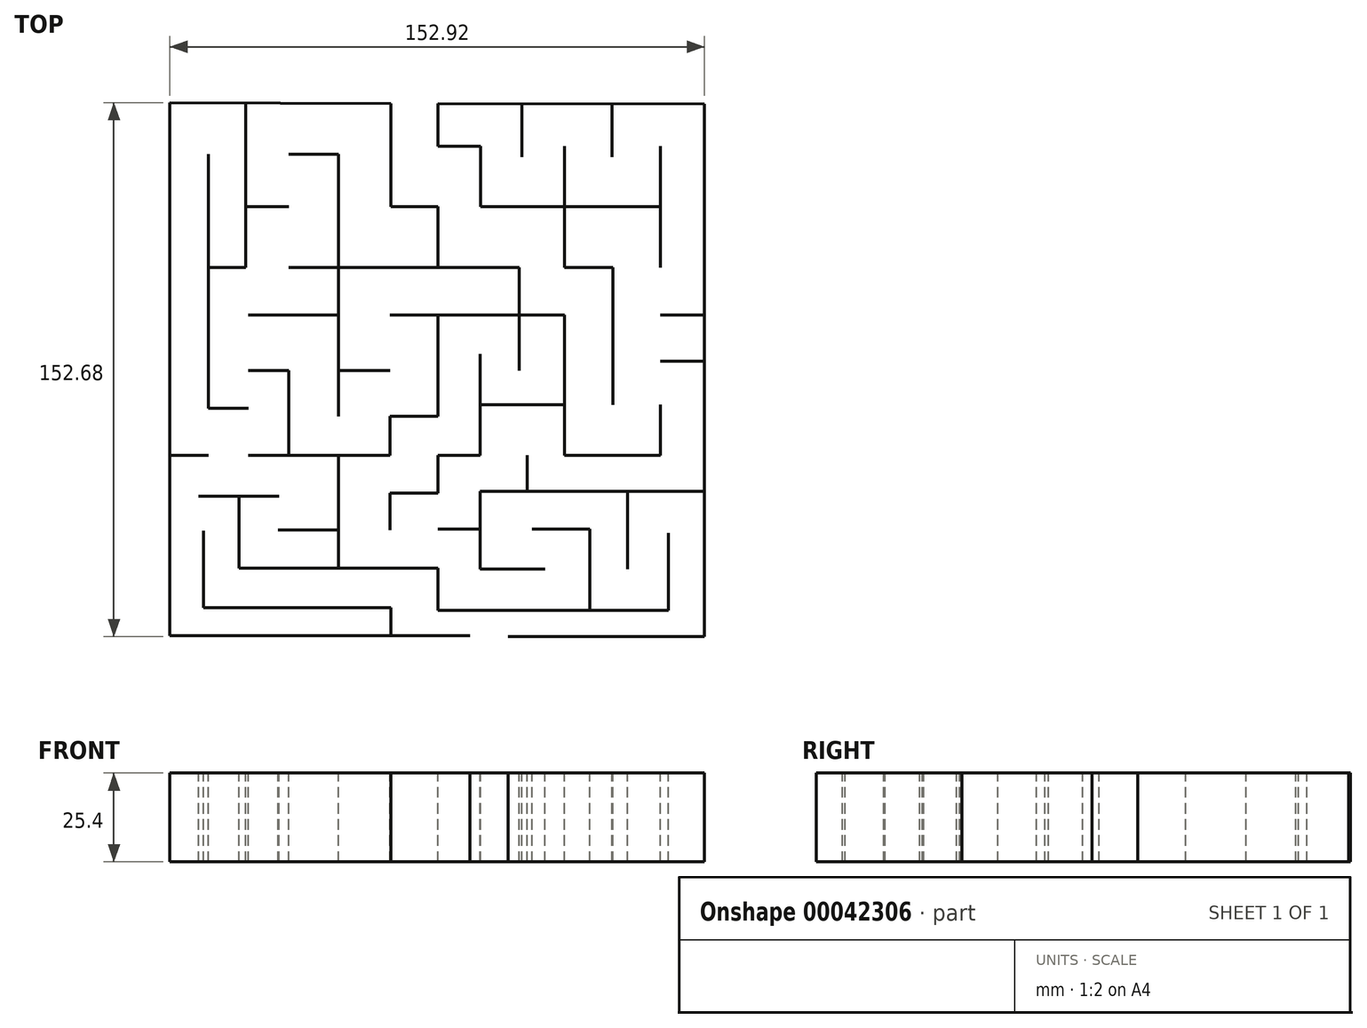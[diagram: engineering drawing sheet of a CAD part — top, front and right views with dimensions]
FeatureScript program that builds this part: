
annotation { "Feature Type Name" : "Feature", "Feature Type Description" : "" }
export const myFeature = defineFeature(function(context is Context, id is Id, definition is map)
    precondition{}
    {
        {
            var Q0;
            Q0=qCreatedBy(makeId("Top.planeOp"),FACE);
            var sketch = newSketch(context, id + "F0", { "sketchPlane" : qUnion([Q0])});
            skLineSegment(sketch, "E0", {"start": v(-76.69, 76.57) * mm, "end": v(-76.69, -75.88) * mm});
            skLineSegment(sketch, "E1", {"start": v(-76.69, -75.88) * mm, "end": v(9.06, -75.88) * mm});
            skLineSegment(sketch, "E2", {"start": v(-13.49, -75.88) * mm, "end": v(-13.49, -67.9) * mm});
            skLineSegment(sketch, "E3", {"start": v(-13.49, -67.9) * mm, "end": v(-67.06, -67.9) * mm});
            skLineSegment(sketch, "E4", {"start": v(-67.06, -67.9) * mm, "end": v(-67.06, -45.85) * mm});
            skLineSegment(sketch, "E5", {"start": v(-68.43, -36) * mm, "end": v(-45.46, -36) * mm});
            skLineSegment(sketch, "E6", {"start": v(-56.95, -36) * mm, "end": v(-56.95, -56.53) * mm});
            skLineSegment(sketch, "E7", {"start": v(-56.95, -56.53) * mm, "end": v(0, -56.53) * mm});
            skLineSegment(sketch, "E8", {"start": v(0, -56.53) * mm, "end": v(0, -68.67) * mm});
            skLineSegment(sketch, "E9", {"start": v(0, -68.67) * mm, "end": v(65.91, -68.67) * mm});
            skLineSegment(sketch, "E10", {"start": v(65.91, -68.67) * mm, "end": v(65.91, -46.54) * mm});
            skLineSegment(sketch, "E11", {"start": v(20.06, -76.11) * mm, "end": v(76.23, -76.11) * mm});
            skLineSegment(sketch, "E12", {"start": v(76.23, -76.11) * mm, "end": v(76.23, 76.11) * mm});
            skLineSegment(sketch, "E13", {"start": v(43.44, -68.67) * mm, "end": v(43.44, -45.42) * mm});
            skLineSegment(sketch, "E14", {"start": v(43.44, -45.42) * mm, "end": v(26.94, -45.42) * mm});
            skLineSegment(sketch, "E15", {"start": v(30.6, -56.86) * mm, "end": v(12.08, -56.86) * mm});
            skLineSegment(sketch, "E16", {"start": v(12.08, -56.86) * mm, "end": v(12.08, -34.57) * mm});
            skLineSegment(sketch, "E17", {"start": v(12.08, -34.57) * mm, "end": v(76.23, -34.57) * mm});
            skLineSegment(sketch, "E18", {"start": v(76.23, -34.57) * mm, "end": v(54.22, -34.57) * mm});
            skLineSegment(sketch, "E19", {"start": v(54.22, -34.57) * mm, "end": v(54.22, -56.86) * mm});
            skLineSegment(sketch, "E20", {"start": v(12.08, -45.42) * mm, "end": v(0, -45.42) * mm});
            skLineSegment(sketch, "E21", {"start": v(25.52, -34.57) * mm, "end": v(25.52, -24.24) * mm});
            skLineSegment(sketch, "E22", {"start": v(-28.47, -56.53) * mm, "end": v(-28.47, -24.24) * mm});
            skLineSegment(sketch, "E23", {"start": v(-28.47, -45.68) * mm, "end": v(-45.78, -45.68) * mm});
            skLineSegment(sketch, "E24", {"start": v(-13.75, -45.68) * mm, "end": v(-13.75, -35.08) * mm});
            skLineSegment(sketch, "E25", {"start": v(-13.75, -35.08) * mm, "end": v(0, -35.08) * mm});
            skLineSegment(sketch, "E26", {"start": v(0, -24.24) * mm, "end": v(0, -35.08) * mm});
            skLineSegment(sketch, "E27", {"start": v(0, -24.24) * mm, "end": v(12.08, -24.24) * mm});
            skLineSegment(sketch, "E28", {"start": v(12.08, -24.24) * mm, "end": v(12.08, 4.7) * mm});
            skLineSegment(sketch, "E29", {"start": v(-28.47, -24.24) * mm, "end": v(-13.75, -24.24) * mm});
            skLineSegment(sketch, "E30", {"start": v(-13.75, -24.24) * mm, "end": v(-54.3, -24.24) * mm});
            skLineSegment(sketch, "E31", {"start": v(-76.69, -24.24) * mm, "end": v(-65.67, -24.24) * mm});
            skLineSegment(sketch, "E32", {"start": v(-54.3, -10.8) * mm, "end": v(-65.67, -10.8) * mm});
            skLineSegment(sketch, "E33", {"start": v(-65.67, -10.8) * mm, "end": v(-65.67, 61.79) * mm});
            skLineSegment(sketch, "E34", {"start": v(-54.3, 0) * mm, "end": v(-42.68, 0) * mm});
            skLineSegment(sketch, "E35", {"start": v(-42.68, 0) * mm, "end": v(-42.68, -24.24) * mm});
            skLineSegment(sketch, "E36", {"start": v(-13.75, -24.24) * mm, "end": v(-13.75, -13.13) * mm});
            skLineSegment(sketch, "E37", {"start": v(-13.75, -13.13) * mm, "end": v(0, -13.13) * mm});
            skLineSegment(sketch, "E38", {"start": v(0, -13.13) * mm, "end": v(0, 15.8) * mm});
            skLineSegment(sketch, "E39", {"start": v(12.08, -9.77) * mm, "end": v(36.1, -9.77) * mm});
            skLineSegment(sketch, "E40", {"start": v(36.1, -9.77) * mm, "end": v(36.1, -24.24) * mm});
            skLineSegment(sketch, "E41", {"start": v(36.1, -24.24) * mm, "end": v(63.62, -24.24) * mm});
            skLineSegment(sketch, "E42", {"start": v(63.62, -24.24) * mm, "end": v(63.62, -9.77) * mm});
            skLineSegment(sketch, "E43", {"start": v(50.06, -9.77) * mm, "end": v(50.06, 29.5) * mm});
            skLineSegment(sketch, "E44", {"start": v(50.06, 29.5) * mm, "end": v(36.1, 29.5) * mm});
            skLineSegment(sketch, "E45", {"start": v(36.1, 29.5) * mm, "end": v(36.1, 64.11) * mm});
            skLineSegment(sketch, "E46", {"start": v(76.23, 15.8) * mm, "end": v(63.62, 15.8) * mm});
            skLineSegment(sketch, "E47", {"start": v(76.23, 2.7) * mm, "end": v(63.62, 2.7) * mm});
            skLineSegment(sketch, "E48", {"start": v(63.62, 64.11) * mm, "end": v(63.62, 29.5) * mm});
            skLineSegment(sketch, "E49", {"start": v(63.62, 46.8) * mm, "end": v(12.16, 46.8) * mm});
            skLineSegment(sketch, "E50", {"start": v(12.16, 46.8) * mm, "end": v(12.16, 64.11) * mm});
            skLineSegment(sketch, "E51", {"start": v(12.16, 64.11) * mm, "end": v(0, 64.11) * mm});
            skLineSegment(sketch, "E52", {"start": v(0, 64.11) * mm, "end": v(0, 76.25) * mm});
            skLineSegment(sketch, "E53", {"start": v(0, 76.25) * mm, "end": v(76.23, 76.11) * mm});
            skLineSegment(sketch, "E54", {"start": v(23.97, 76.2) * mm, "end": v(23.97, 61.01) * mm});
            skLineSegment(sketch, "E55", {"start": v(49.8, 76.16) * mm, "end": v(49.8, 61.01) * mm});
            skLineSegment(sketch, "E56", {"start": v(36.1, -9.77) * mm, "end": v(36.1, 15.8) * mm});
            skLineSegment(sketch, "E57", {"start": v(36.1, 15.8) * mm, "end": v(-13.75, 15.8) * mm});
            skLineSegment(sketch, "E58", {"start": v(23.2, 0) * mm, "end": v(23.2, 29.5) * mm});
            skLineSegment(sketch, "E59", {"start": v(23.2, 29.5) * mm, "end": v(-42.68, 29.5) * mm});
            skLineSegment(sketch, "E60", {"start": v(0, 29.5) * mm, "end": v(0, 46.8) * mm});
            skLineSegment(sketch, "E61", {"start": v(0, 46.8) * mm, "end": v(-13.49, 46.8) * mm});
            skLineSegment(sketch, "E62", {"start": v(-13.49, 46.8) * mm, "end": v(-13.49, 76.25) * mm});
            skLineSegment(sketch, "E63", {"start": v(-13.49, 76.25) * mm, "end": v(-76.69, 76.57) * mm});
            skLineSegment(sketch, "E64", {"start": v(-42.68, 61.79) * mm, "end": v(-28.47, 61.79) * mm});
            skLineSegment(sketch, "E65", {"start": v(-28.47, 61.79) * mm, "end": v(-28.47, -13.13) * mm});
            skLineSegment(sketch, "E66", {"start": v(-65.67, 29.5) * mm, "end": v(-55.08, 29.5) * mm});
            skLineSegment(sketch, "E67", {"start": v(-55.08, 29.5) * mm, "end": v(-55.08, 76.46) * mm});
            skLineSegment(sketch, "E68", {"start": v(-55.08, 46.8) * mm, "end": v(-42.68, 46.8) * mm});
            skLineSegment(sketch, "E69", {"start": v(-28.47, 15.8) * mm, "end": v(-54.3, 15.8) * mm});
            skLineSegment(sketch, "E70", {"start": v(-28.47, 0) * mm, "end": v(-13.75, 0) * mm});
            skSolve(sketch);
        }
        {
            var Q0;
            Q0=sQuery(id+"F0.wireOp",EDGE,"E59");
            extrude(context, id + "F1", {"bodyType" : ToolBodyType.SURFACE, "surfaceEntities" : qUnion([Q0]), "depth" : 25.4 * mm});
        }
        {
            var Q0;
            Q0=sQuery(id+"F0.wireOp",EDGE,"E51");
            extrude(context, id + "F2", {"bodyType" : ToolBodyType.SURFACE, "surfaceEntities" : qUnion([Q0]), "depth" : 25.4 * mm});
        }
        {
            var Q0;
            Q0=sQuery(id+"F0.wireOp",EDGE,"E53");
            extrude(context, id + "F3", {"bodyType" : ToolBodyType.SURFACE, "surfaceEntities" : qUnion([Q0]), "depth" : 25.4 * mm});
        }
        {
            var Q0;
            Q0=sQuery(id+"F0.wireOp",EDGE,"E54");
            extrude(context, id + "F4", {"bodyType" : ToolBodyType.SURFACE, "surfaceEntities" : qUnion([Q0]), "depth" : 25.4 * mm});
        }
        {
            var Q0;
            Q0=sQuery(id+"F0.wireOp",EDGE,"E45");
            extrude(context, id + "F5", {"bodyType" : ToolBodyType.SURFACE, "surfaceEntities" : qUnion([Q0]), "depth" : 25.4 * mm});
        }
        {
            var Q0;
            Q0=sQuery(id+"F0.wireOp",EDGE,"E55");
            extrude(context, id + "F6", {"bodyType" : ToolBodyType.SURFACE, "surfaceEntities" : qUnion([Q0]), "depth" : 25.4 * mm});
        }
        {
            var Q0;
            Q0=sQuery(id+"F0.wireOp",EDGE,"E12");
            extrude(context, id + "F7", {"bodyType" : ToolBodyType.SURFACE, "surfaceEntities" : qUnion([Q0]), "depth" : 25.4 * mm});
        }
        {
            var Q0;
            Q0=sQuery(id+"F0.wireOp",EDGE,"E48");
            extrude(context, id + "F8", {"bodyType" : ToolBodyType.SURFACE, "surfaceEntities" : qUnion([Q0]), "depth" : 25.4 * mm});
        }
        {
            var Q0;
            Q0=sQuery(id+"F0.wireOp",EDGE,"E49");
            extrude(context, id + "F9", {"bodyType" : ToolBodyType.SURFACE, "surfaceEntities" : qUnion([Q0]), "depth" : 25.4 * mm});
        }
        {
            var Q0;
            Q0=sQuery(id+"F0.wireOp",EDGE,"E44");
            extrude(context, id + "F10", {"bodyType" : ToolBodyType.SURFACE, "surfaceEntities" : qUnion([Q0]), "depth" : 25.4 * mm});
        }
        {
            var Q0;
            Q0=sQuery(id+"F0.wireOp",EDGE,"E43");
            extrude(context, id + "F11", {"bodyType" : ToolBodyType.SURFACE, "surfaceEntities" : qUnion([Q0]), "depth" : 25.4 * mm});
        }
        {
            var Q0;
            Q0=sQuery(id+"F0.wireOp",EDGE,"E52");
            extrude(context, id + "F12", {"bodyType" : ToolBodyType.SURFACE, "surfaceEntities" : qUnion([Q0]), "depth" : 25.4 * mm});
        }
        {
            var Q0;
            Q0=sQuery(id+"F0.wireOp",EDGE,"E50");
            extrude(context, id + "F13", {"bodyType" : ToolBodyType.SURFACE, "surfaceEntities" : qUnion([Q0]), "depth" : 25.4 * mm});
        }
        {
            var Q0;
            Q0=sQuery(id+"F0.wireOp",EDGE,"E62");
            extrude(context, id + "F14", {"bodyType" : ToolBodyType.SURFACE, "surfaceEntities" : qUnion([Q0]), "depth" : 25.4 * mm});
        }
        {
            var Q0;
            Q0=sQuery(id+"F0.wireOp",EDGE,"E61");
            extrude(context, id + "F15", {"bodyType" : ToolBodyType.SURFACE, "surfaceEntities" : qUnion([Q0]), "depth" : 25.4 * mm});
        }
        {
            var Q0;
            Q0=sQuery(id+"F0.wireOp",EDGE,"E60");
            extrude(context, id + "F16", {"bodyType" : ToolBodyType.SURFACE, "surfaceEntities" : qUnion([Q0]), "depth" : 25.4 * mm});
        }
        {
            var Q0;
            Q0=sQuery(id+"F0.wireOp",EDGE,"E58");
            extrude(context, id + "F17", {"bodyType" : ToolBodyType.SURFACE, "surfaceEntities" : qUnion([Q0]), "depth" : 25.4 * mm});
        }
        {
            var Q0;
            Q0=sQuery(id+"F0.wireOp",EDGE,"E57");
            extrude(context, id + "F18", {"bodyType" : ToolBodyType.SURFACE, "surfaceEntities" : qUnion([Q0]), "depth" : 25.4 * mm});
        }
        {
            var Q0;
            Q0=sQuery(id+"F0.wireOp",EDGE,"E65");
            extrude(context, id + "F19", {"bodyType" : ToolBodyType.SURFACE, "surfaceEntities" : qUnion([Q0]), "depth" : 25.4 * mm});
        }
        {
            var Q0;
            Q0=sQuery(id+"F0.wireOp",EDGE,"E38");
            extrude(context, id + "F20", {"bodyType" : ToolBodyType.SURFACE, "surfaceEntities" : qUnion([Q0]), "depth" : 25.4 * mm});
        }
        {
            var Q0;
            Q0=sQuery(id+"F0.wireOp",EDGE,"E64");
            extrude(context, id + "F21", {"bodyType" : ToolBodyType.SURFACE, "surfaceEntities" : qUnion([Q0]), "depth" : 25.4 * mm});
        }
        {
            var Q0;
            Q0=sQuery(id+"F0.wireOp",EDGE,"E63");
            extrude(context, id + "F22", {"bodyType" : ToolBodyType.SURFACE, "surfaceEntities" : qUnion([Q0]), "depth" : 25.4 * mm});
        }
        {
            var Q0;
            Q0=sQuery(id+"F0.wireOp",EDGE,"E0");
            extrude(context, id + "F23", {"bodyType" : ToolBodyType.SURFACE, "surfaceEntities" : qUnion([Q0]), "depth" : 25.4 * mm});
        }
        {
            var Q0;
            Q0=sQuery(id+"F0.wireOp",EDGE,"E67");
            extrude(context, id + "F24", {"bodyType" : ToolBodyType.SURFACE, "surfaceEntities" : qUnion([Q0]), "depth" : 25.4 * mm});
        }
        {
            var Q0;
            Q0=sQuery(id+"F0.wireOp",EDGE,"E33");
            extrude(context, id + "F25", {"bodyType" : ToolBodyType.SURFACE, "surfaceEntities" : qUnion([Q0]), "depth" : 25.4 * mm});
        }
        {
            var Q0;
            Q0=sQuery(id+"F0.wireOp",EDGE,"E66");
            extrude(context, id + "F26", {"bodyType" : ToolBodyType.SURFACE, "surfaceEntities" : qUnion([Q0]), "depth" : 25.4 * mm});
        }
        {
            var Q0;
            Q0=sQuery(id+"F0.wireOp",EDGE,"E68");
            extrude(context, id + "F27", {"bodyType" : ToolBodyType.SURFACE, "surfaceEntities" : qUnion([Q0]), "depth" : 25.4 * mm});
        }
        {
            var Q0;
            Q0=sQuery(id+"F0.wireOp",EDGE,"E69");
            extrude(context, id + "F28", {"bodyType" : ToolBodyType.SURFACE, "surfaceEntities" : qUnion([Q0]), "depth" : 25.4 * mm});
        }
        {
            var Q0;
            Q0=sQuery(id+"F0.wireOp",EDGE,"E34");
            extrude(context, id + "F29", {"bodyType" : ToolBodyType.SURFACE, "surfaceEntities" : qUnion([Q0]), "depth" : 25.4 * mm});
        }
        {
            var Q0;
            Q0=sQuery(id+"F0.wireOp",EDGE,"E35");
            extrude(context, id + "F30", {"bodyType" : ToolBodyType.SURFACE, "surfaceEntities" : qUnion([Q0]), "depth" : 25.4 * mm});
        }
        {
            var Q0;
            Q0=sQuery(id+"F0.wireOp",EDGE,"E32");
            extrude(context, id + "F31", {"bodyType" : ToolBodyType.SURFACE, "surfaceEntities" : qUnion([Q0]), "depth" : 25.4 * mm});
        }
        {
            var Q0;
            Q0=sQuery(id+"F0.wireOp",EDGE,"E70");
            extrude(context, id + "F32", {"bodyType" : ToolBodyType.SURFACE, "surfaceEntities" : qUnion([Q0]), "depth" : 25.4 * mm});
        }
        {
            var Q0;
            Q0=sQuery(id+"F0.wireOp",EDGE,"E46");
            var Q1;
            Q1=sQuery(id+"F0.wireOp",EDGE,"E47");
            extrude(context, id + "F33", {"bodyType" : ToolBodyType.SURFACE, "surfaceEntities" : qUnion([Q0, Q1]), "depth" : 25.4 * mm});
        }
        {
            var Q0;
            Q0=sQuery(id+"F0.wireOp",EDGE,"E30");
            extrude(context, id + "F34", {"bodyType" : ToolBodyType.SURFACE, "surfaceEntities" : qUnion([Q0]), "depth" : 25.4 * mm});
        }
        {
            var Q0;
            Q0=sQuery(id+"F0.wireOp",EDGE,"E37");
            var Q1;
            Q1=sQuery(id+"F0.wireOp",EDGE,"E38");
            var Q2;
            Q2=sQuery(id+"F0.wireOp",EDGE,"E28");
            var Q3;
            Q3=sQuery(id+"F0.wireOp",EDGE,"E27");
            var Q4;
            Q4=sQuery(id+"F0.wireOp",EDGE,"E36");
            var Q5;
            Q5=sQuery(id+"F0.wireOp",EDGE,"E26");
            var Q6;
            Q6=sQuery(id+"F0.wireOp",EDGE,"E25");
            extrude(context, id + "F35", {"bodyType" : ToolBodyType.SURFACE, "surfaceEntities" : qUnion([Q0, Q1, Q2, Q3, Q4, Q5, Q6]), "depth" : 25.4 * mm});
        }
        {
            var Q0;
            Q0=sQuery(id+"F0.wireOp",EDGE,"E22");
            extrude(context, id + "F36", {"bodyType" : ToolBodyType.SURFACE, "surfaceEntities" : qUnion([Q0]), "depth" : 25.4 * mm});
        }
        {
            var Q0;
            Q0=sQuery(id+"F0.wireOp",EDGE,"E30");
            extrude(context, id + "F37", {"bodyType" : ToolBodyType.SURFACE, "surfaceEntities" : qUnion([Q0]), "depth" : 25.4 * mm});
        }
        {
            var Q0;
            Q0=sQuery(id+"F0.wireOp",EDGE,"E23");
            extrude(context, id + "F38", {"bodyType" : ToolBodyType.SURFACE, "surfaceEntities" : qUnion([Q0]), "depth" : 25.4 * mm});
        }
        {
            var Q0;
            Q0=sQuery(id+"F0.wireOp",EDGE,"E31");
            extrude(context, id + "F39", {"bodyType" : ToolBodyType.SURFACE, "surfaceEntities" : qUnion([Q0]), "depth" : 25.4 * mm});
        }
        {
            var Q0;
            Q0=sQuery(id+"F0.wireOp",EDGE,"E5");
            extrude(context, id + "F40", {"bodyType" : ToolBodyType.SURFACE, "surfaceEntities" : qUnion([Q0]), "depth" : 25.4 * mm});
        }
        {
            var Q0;
            Q0=sQuery(id+"F0.wireOp",EDGE,"E4");
            extrude(context, id + "F41", {"bodyType" : ToolBodyType.SURFACE, "surfaceEntities" : qUnion([Q0]), "depth" : 25.4 * mm});
        }
        {
            var Q0;
            Q0=sQuery(id+"F0.wireOp",EDGE,"E6");
            extrude(context, id + "F42", {"bodyType" : ToolBodyType.SURFACE, "surfaceEntities" : qUnion([Q0]), "depth" : 25.4 * mm});
        }
        {
            var Q0;
            Q0=sQuery(id+"F0.wireOp",EDGE,"E3");
            extrude(context, id + "F43", {"bodyType" : ToolBodyType.SURFACE, "surfaceEntities" : qUnion([Q0]), "depth" : 25.4 * mm});
        }
        {
            var Q0;
            Q0=sQuery(id+"F0.wireOp",EDGE,"E7");
            extrude(context, id + "F44", {"bodyType" : ToolBodyType.SURFACE, "surfaceEntities" : qUnion([Q0]), "depth" : 25.4 * mm});
        }
        {
            var Q0;
            Q0=sQuery(id+"F0.wireOp",EDGE,"E1");
            extrude(context, id + "F45", {"bodyType" : ToolBodyType.SURFACE, "surfaceEntities" : qUnion([Q0]), "depth" : 25.4 * mm});
        }
        {
            var Q0;
            Q0=sQuery(id+"F0.wireOp",EDGE,"E2");
            extrude(context, id + "F46", {"bodyType" : ToolBodyType.SURFACE, "surfaceEntities" : qUnion([Q0]), "depth" : 25.4 * mm});
        }
        {
            var Q0;
            Q0=sQuery(id+"F0.wireOp",EDGE,"E24");
            extrude(context, id + "F47", {"bodyType" : ToolBodyType.SURFACE, "surfaceEntities" : qUnion([Q0]), "depth" : 25.4 * mm});
        }
        {
            var Q0;
            Q0=sQuery(id+"F0.wireOp",EDGE,"E39");
            extrude(context, id + "F48", {"bodyType" : ToolBodyType.SURFACE, "surfaceEntities" : qUnion([Q0]), "depth" : 25.4 * mm});
        }
        {
            var Q0;
            Q0=sQuery(id+"F0.wireOp",EDGE,"E56");
            extrude(context, id + "F49", {"bodyType" : ToolBodyType.SURFACE, "surfaceEntities" : qUnion([Q0]), "depth" : 25.4 * mm});
        }
        {
            var Q0;
            Q0=sQuery(id+"F0.wireOp",EDGE,"E40");
            extrude(context, id + "F50", {"bodyType" : ToolBodyType.SURFACE, "surfaceEntities" : qUnion([Q0]), "depth" : 25.4 * mm});
        }
        {
            var Q0;
            Q0=sQuery(id+"F0.wireOp",EDGE,"E41");
            extrude(context, id + "F51", {"bodyType" : ToolBodyType.SURFACE, "surfaceEntities" : qUnion([Q0]), "depth" : 25.4 * mm});
        }
        {
            var Q0;
            Q0=sQuery(id+"F0.wireOp",EDGE,"E42");
            extrude(context, id + "F52", {"bodyType" : ToolBodyType.SURFACE, "surfaceEntities" : qUnion([Q0]), "depth" : 25.4 * mm});
        }
        {
            var Q0;
            Q0=sQuery(id+"F0.wireOp",EDGE,"E21");
            extrude(context, id + "F53", {"bodyType" : ToolBodyType.SURFACE, "surfaceEntities" : qUnion([Q0]), "depth" : 25.4 * mm});
        }
        {
            var Q0;
            Q0=sQuery(id+"F0.wireOp",EDGE,"E17");
            extrude(context, id + "F54", {"bodyType" : ToolBodyType.SURFACE, "surfaceEntities" : qUnion([Q0]), "depth" : 25.4 * mm});
        }
        {
            var Q0;
            Q0=sQuery(id+"F0.wireOp",EDGE,"E19");
            extrude(context, id + "F55", {"bodyType" : ToolBodyType.SURFACE, "surfaceEntities" : qUnion([Q0]), "depth" : 25.4 * mm});
        }
        {
            var Q0;
            Q0=sQuery(id+"F0.wireOp",EDGE,"E20");
            extrude(context, id + "F56", {"bodyType" : ToolBodyType.SURFACE, "surfaceEntities" : qUnion([Q0]), "depth" : 25.4 * mm});
        }
        {
            var Q0;
            Q0=sQuery(id+"F0.wireOp",EDGE,"E16");
            extrude(context, id + "F57", {"bodyType" : ToolBodyType.SURFACE, "surfaceEntities" : qUnion([Q0]), "depth" : 25.4 * mm});
        }
        {
            var Q0;
            Q0=sQuery(id+"F0.wireOp",EDGE,"E15");
            extrude(context, id + "F58", {"bodyType" : ToolBodyType.SURFACE, "surfaceEntities" : qUnion([Q0]), "depth" : 25.4 * mm});
        }
        {
            var Q0;
            Q0=sQuery(id+"F0.wireOp",EDGE,"E14");
            extrude(context, id + "F59", {"bodyType" : ToolBodyType.SURFACE, "surfaceEntities" : qUnion([Q0]), "depth" : 25.4 * mm});
        }
        {
            var Q0;
            Q0=sQuery(id+"F0.wireOp",EDGE,"E13");
            extrude(context, id + "F60", {"bodyType" : ToolBodyType.SURFACE, "surfaceEntities" : qUnion([Q0]), "depth" : 25.4 * mm});
        }
        {
            var Q0;
            Q0=sQuery(id+"F0.wireOp",EDGE,"E8");
            extrude(context, id + "F61", {"bodyType" : ToolBodyType.SURFACE, "surfaceEntities" : qUnion([Q0]), "depth" : 25.4 * mm});
        }
        {
            var Q0;
            Q0=sQuery(id+"F0.wireOp",EDGE,"E9");
            extrude(context, id + "F62", {"bodyType" : ToolBodyType.SURFACE, "surfaceEntities" : qUnion([Q0]), "depth" : 25.4 * mm});
        }
        {
            var Q0;
            Q0=sQuery(id+"F0.wireOp",EDGE,"E10");
            extrude(context, id + "F63", {"bodyType" : ToolBodyType.SURFACE, "surfaceEntities" : qUnion([Q0]), "depth" : 25.4 * mm});
        }
        {
            var Q0;
            Q0=sQuery(id+"F0.wireOp",EDGE,"E11");
            extrude(context, id + "F64", {"bodyType" : ToolBodyType.SURFACE, "surfaceEntities" : qUnion([Q0]), "depth" : 25.4 * mm});
        }
    });
